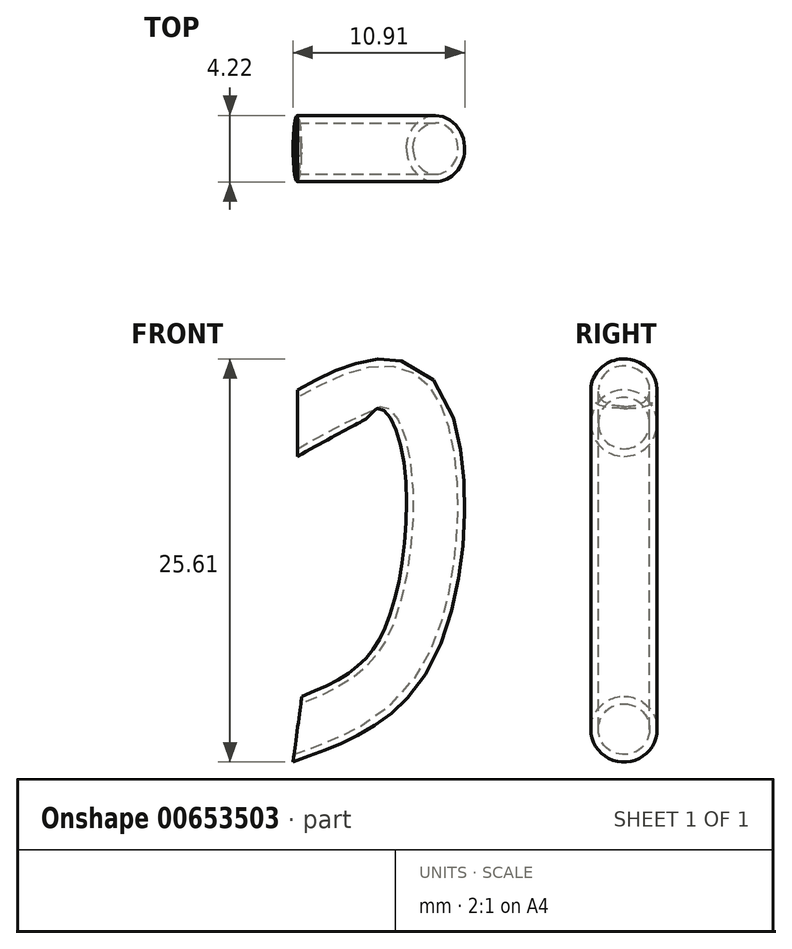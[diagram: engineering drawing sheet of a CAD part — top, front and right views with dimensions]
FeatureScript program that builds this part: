
annotation { "Feature Type Name" : "Feature", "Feature Type Description" : "" }
export const myFeature = defineFeature(function(context is Context, id is Id, definition is map)
    precondition{}
    {
        {
            var Q0;
            Q0=qCreatedBy(makeId("Right.planeOp"),FACE);
            var sketch = newSketch(context, id + "F0", { "sketchPlane" : qUnion([Q0])});
            skCircle(sketch, "E0", {"center": v(0, 22.6) * mm, "radius": 1.63 * mm});
            skCircle(sketch, "E1.0", {"center": v(0, 22.6) * mm, "radius": 2.1 * mm});
            skSolve(sketch);
        }
        {
            var Q0;
            Q0=qCreatedBy(makeId("Front.planeOp"),FACE);
            var sketch = newSketch(context, id + "F1", { "sketchPlane" : qUnion([Q0])});
            skFitSpline(sketch, "E2", {"points": [v(0, 22.7) * mm, v(7.14, 24.2) * mm, v(7.24, 8.76) * mm, v(0, 3.07) * mm], "startDerivative": vector(29.7, 16.26) * mm, "endDerivative": vector(-26.8, -10.34) * mm});
            skSolve(sketch);
        }
        {
            var Q0;
            Q0=makeQuery(id+"F0.imprint","IMPRINT",FACE,{"disambiguationData":[TD([[makeQuery(id+"F0.imprint","IMPRINT",EDGE,{"derivedFrom":sQuery(id+"F0.wireOp",EDGE,"E0")}),-1.0]])]});
            var Q1;
            Q1=sQuery(id+"F1.wireOp",EDGE,"E2");
            sweep(context, id + "F2", {"profiles" : qUnion([Q0]), "path" : qUnion([Q1])});
        }
    });
